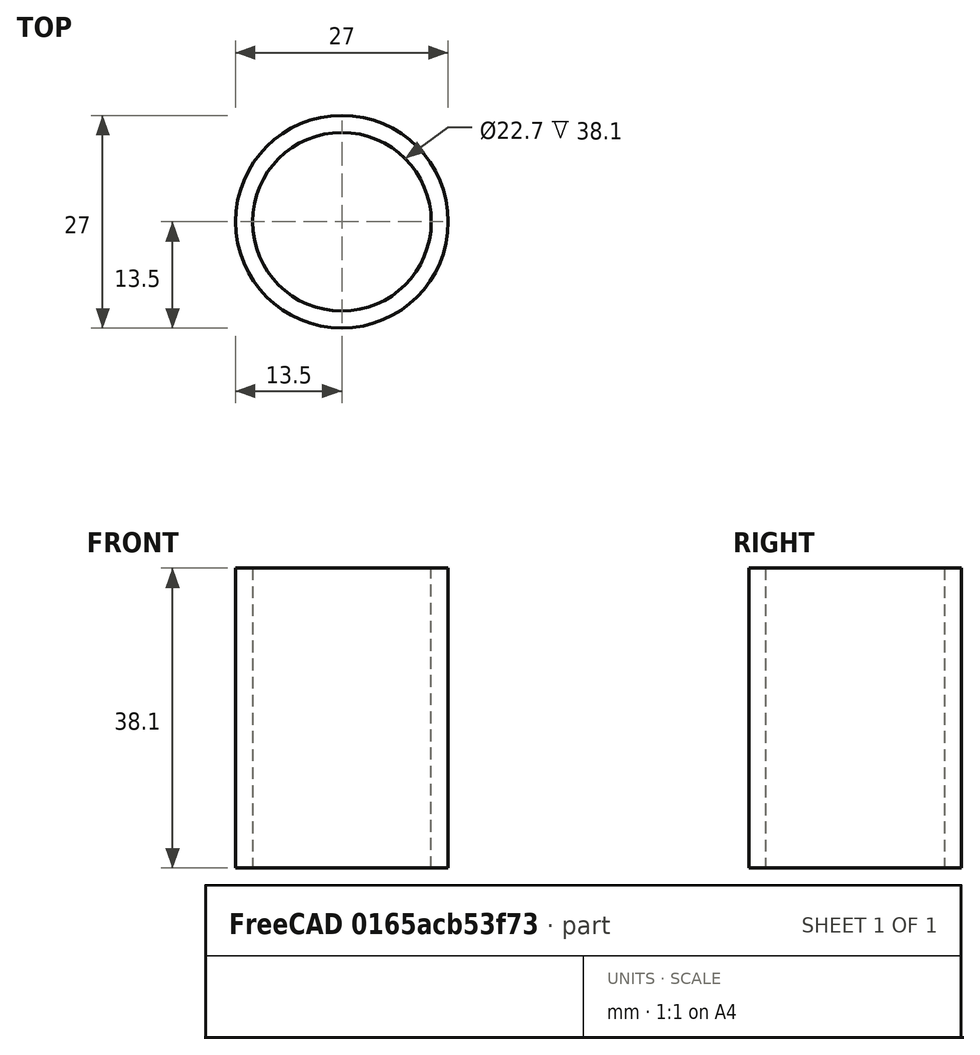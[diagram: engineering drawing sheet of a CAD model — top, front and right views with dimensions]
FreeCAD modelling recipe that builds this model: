
FCSTD DOCUMENT  (FreeCAD 0.20R29177 +426 (Git))
Label: SlipRingSpacer
License: All rights reserved
LicenseURL: http://en.wikipedia.org/wiki/All_rights_reserved
objects: Sketcher::SketchObject×1, PartDesign::Pad×1, PartDesign::Body×1
note: 4 computed .brp shape members not serialized (recipe doc carries the construction recipe); baked Part::Feature solids carry a one-line shape summary decoded from their .brp

FEATURE [Sketcher::SketchObject] Sketch
  FullyConstrained = true
  MapMode = 5
  Support = -> [XY_Plane]
  sketch-geometry (2):
    g0: Circle CenterX=0 CenterY=0 CenterZ=0 NormalX=0 NormalY=0 NormalZ=1 AngleXU=0 Radius=11.35
    g1: Circle CenterX=0 CenterY=0 CenterZ=0 NormalX=0 NormalY=0 NormalZ=1 AngleXU=0 Radius=13.5
  constraints (4):
    c: Coincident(g0,g-1)
    c: Coincident(g1,g0)
    c: Diameter(g0) = 22.7
    c: Diameter(g1) = 27
FEATURE [PartDesign::Pad] Pad
  Direction = (0,0,1)
  Length = 38.1
  Length2 = 10
  Profile = -> Sketch
  ReferenceAxis = -> Sketch [N_Axis]
  Type = 0
FEATURE [PartDesign::Body] Body
  Group = -> [Sketch,Pad]
  Origin = -> Origin
  Tip = -> Pad
